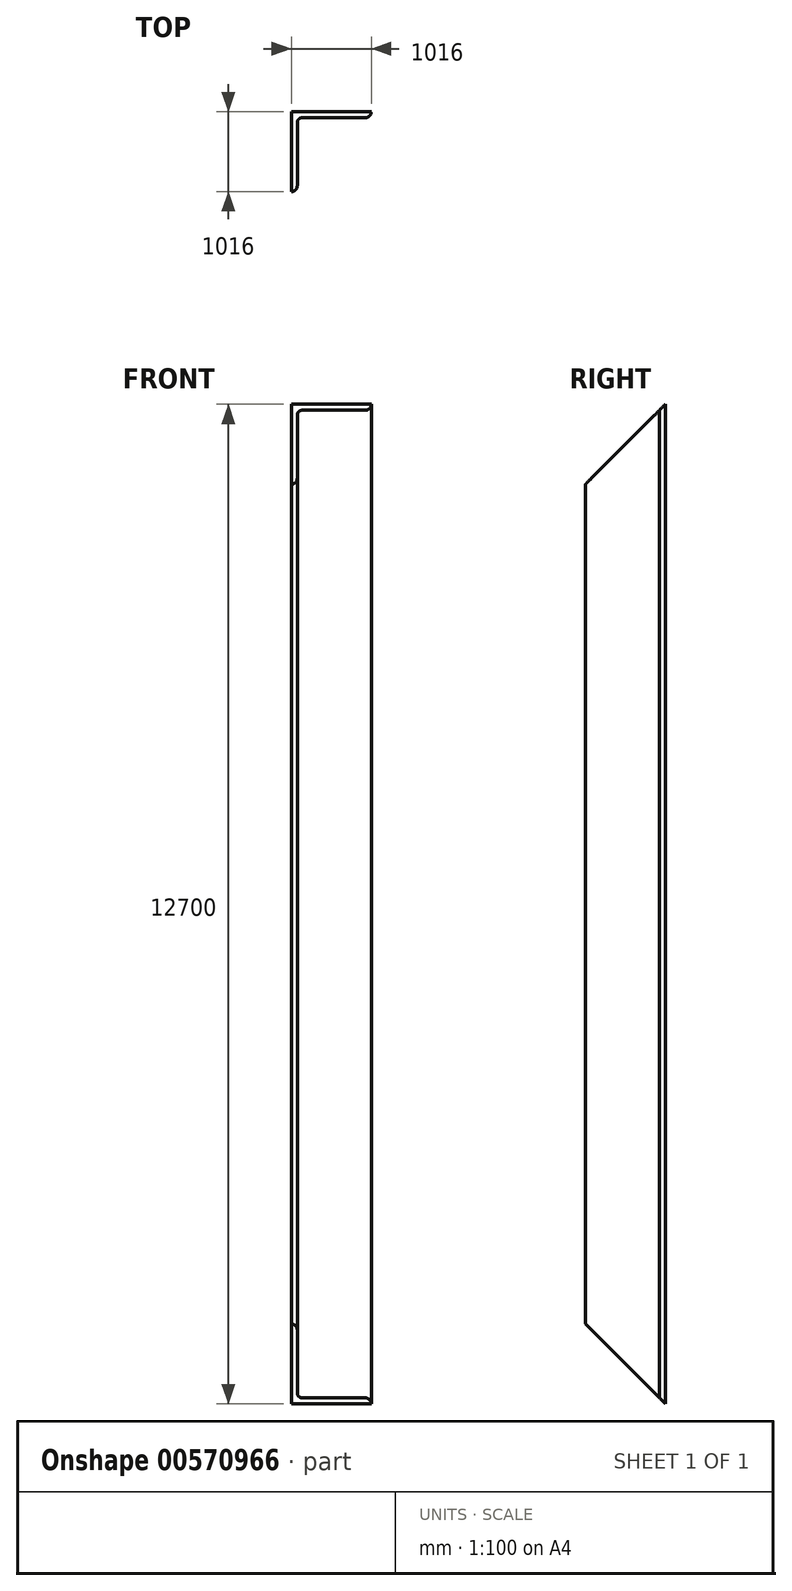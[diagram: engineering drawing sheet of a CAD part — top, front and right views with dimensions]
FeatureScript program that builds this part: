
annotation { "Feature Type Name" : "Feature", "Feature Type Description" : "" }
export const myFeature = defineFeature(function(context is Context, id is Id, definition is map)
    precondition{}
    {
        {
            var Q0;
            Q0=qCreatedBy(makeId("Top.planeOp"),FACE);
            var sketch = newSketch(context, id + "F0", { "sketchPlane" : qUnion([Q0])});
            skLineSegment(sketch, "E0", {"start": v(0, 0) * mm, "end": v(1016, 0) * mm});
            skLineSegment(sketch, "E1", {"start": v(0, 0) * mm, "end": v(0, -1016) * mm});
            skLineSegment(sketch, "E2", {"start": v(939.8, -76.2) * mm, "end": v(139.7, -76.2) * mm});
            skLineSegment(sketch, "E3", {"start": v(76.2, -139.7) * mm, "end": v(76.2, -939.8) * mm});
            skArc(sketch, "E4", {"start": v(1016, 0) * mm, "mid": v(993.68, -53.88) * mm, "end": v(939.8, -76.2) * mm});
            skArc(sketch, "E5", {"start": v(76.2, -939.8) * mm, "mid": v(53.88, -993.68) * mm, "end": v(0, -1016) * mm});
            skPoint(sketch, "E6.visualSharp", {"position": v(76.2, -76.2) * mm});
            skArc(sketch, "E6.filletArc", {"start": v(139.7, -76.2) * mm, "mid": v(94.8, -94.8) * mm, "end": v(76.2, -139.7) * mm});
            skSolve(sketch);
        }
        {
            var Q0;
            Q0 = qSketchRegion(id + "F0", true);
            extrude(context, id + "F1", {"entities" : qUnion([Q0]), "depth" : 12700 * mm, "offsetDistance" : 25.4 * mm});
        }
        {
            var Q0;
            Q0=makeQuery(id+"F1.opExtrude","SWEPT_FACE",FACE,{"disambiguationData":[OSD([sQuery(id+"F0.wireOp",EDGE,"E1")])]});
            var sketch = newSketch(context, id + "F2", { "sketchPlane" : qUnion([Q0])});
            skLineSegment(sketch, "E7", {"start": v(0, 0) * mm, "end": v(1558.13, 1558.13) * mm});
            skLineSegment(sketch, "E8", {"start": v(1558.13, 1558.13) * mm, "end": v(2256.78, -992.7) * mm});
            skLineSegment(sketch, "E9", {"start": v(2256.78, -992.7) * mm, "end": v(0, 0) * mm});
            skLineSegment(sketch, "E10", {"start": v(0, 12700) * mm, "end": v(1590.98, 11109.02) * mm});
            skLineSegment(sketch, "E11", {"start": v(1590.98, 11109.02) * mm, "end": v(2495.95, 14632.78) * mm});
            skLineSegment(sketch, "E12", {"start": v(2495.95, 14632.78) * mm, "end": v(0, 12700) * mm});
            skSolve(sketch);
        }
        {
            var Q0;
            Q0 = qSketchRegion(id + "F2", true);
            extrude(context, id + "F3", {"entities" : qUnion([Q0]), "operationType" : NewBodyOperationType.REMOVE, "oppositeDirection" : true, "depth" : 2032 * mm, "offsetDistance" : 25.4 * mm});
        }
    });
